# Revit family: Bathtub_160x70cm_RectangularBathtub_Vitra_NeonSeries_52520001000
name_source: partatom
category: Plumbing Fixtures
revit_build: Autodesk Revit 2017 (Build: 20160225_1515(x64)
units: mm (PartAtom-declared; Revit-internal decimal feet)

## family parameters
Cut with Voids When Loaded = No
Host = Face
OmniClass Number = 23.45.05.14.17
OmniClass Title = Showers
Part Type = Normal
Room Calculation Point = No
Round Connector Dimension = Use Diameter
Shared = Yes

## types (1)
- Bathtub_160x70cm_RectangularBathtub_Vitra_NeonSeries_52520001000
    Article No. (default) = 52520001000
    BIMobject category = Sanitary - Bath & Spas
    CW Connection = No
    Color = White
    Cost = 0 $
    Default Elevation = 0 mm  [stored 0 ft]
    Description = VitrA Neon Rectangular Bathtub
    Design country = Turkey
    HW Connection = No
    IFC Classification = Sanitary Terminal
    Main Material = Acyrlic
    Manufacturer = Vitra
    Manufacturer name = Vitra
    Masterformat 2014 Code = 22 41 19
    Masterformat 2014 Description = Residential Bathtubs
    Model = 52520001000
    MountingType = Floor Mounted
    NBS Referans Code = 35-06-08
    NBS Referans Description = Baths
    Nominal Depth = 700 mm  [stored 2.29659 ft]
    NominalHeight = 560 mm
    NominalWidth = 1600 mm  [stored 5.24934 ft]
    OmniClass Code = 23-31 15 00
    OmniClass Description = Bathtubs
    Primary material = White
    Product SKU = 52520001000
    Product certification = https://vitraglobal.com
    Product data url = https://www.vitraglobal.com
    Product family = Floor Mounted Bathtub
    Product group = Free Standing Bathtub
    Secondary Material = White
    Technical description = https://www.vitraglobal.com
    UNSPSC Code = 30181501
    UNSPSC Description = Bathtubs
    URL = https://www.vitraglobal.com
    Uniclass 1.4 Code = L7211
    Uniclass 1.4 Description = Baths
    Uniclass 2.0 Code = PR-35-06-08
    Uniclass 2.0 Description = Baths
    Uniclass 2015 Code = Pr_40_20_06_08
    Uniclass 2015 Name = Baths
    Uniformat II Code = D2010
    Uniformat II Description = Plumbing Fixtures
    Vent Connection = No
    Warranty Period (Year) = 10 Years
    Waste Connection = Yes
    Weight Net (kg) = 21,370
    Youtube = https://www.youtube.com

note: [stored X ft] marks values corroborated as IEEE doubles in the binary element streams (Revit-internal decimal feet)

## geometry (parser evidence)
native form markers: Sweep x3
no freeform markers — native parametric forms only
